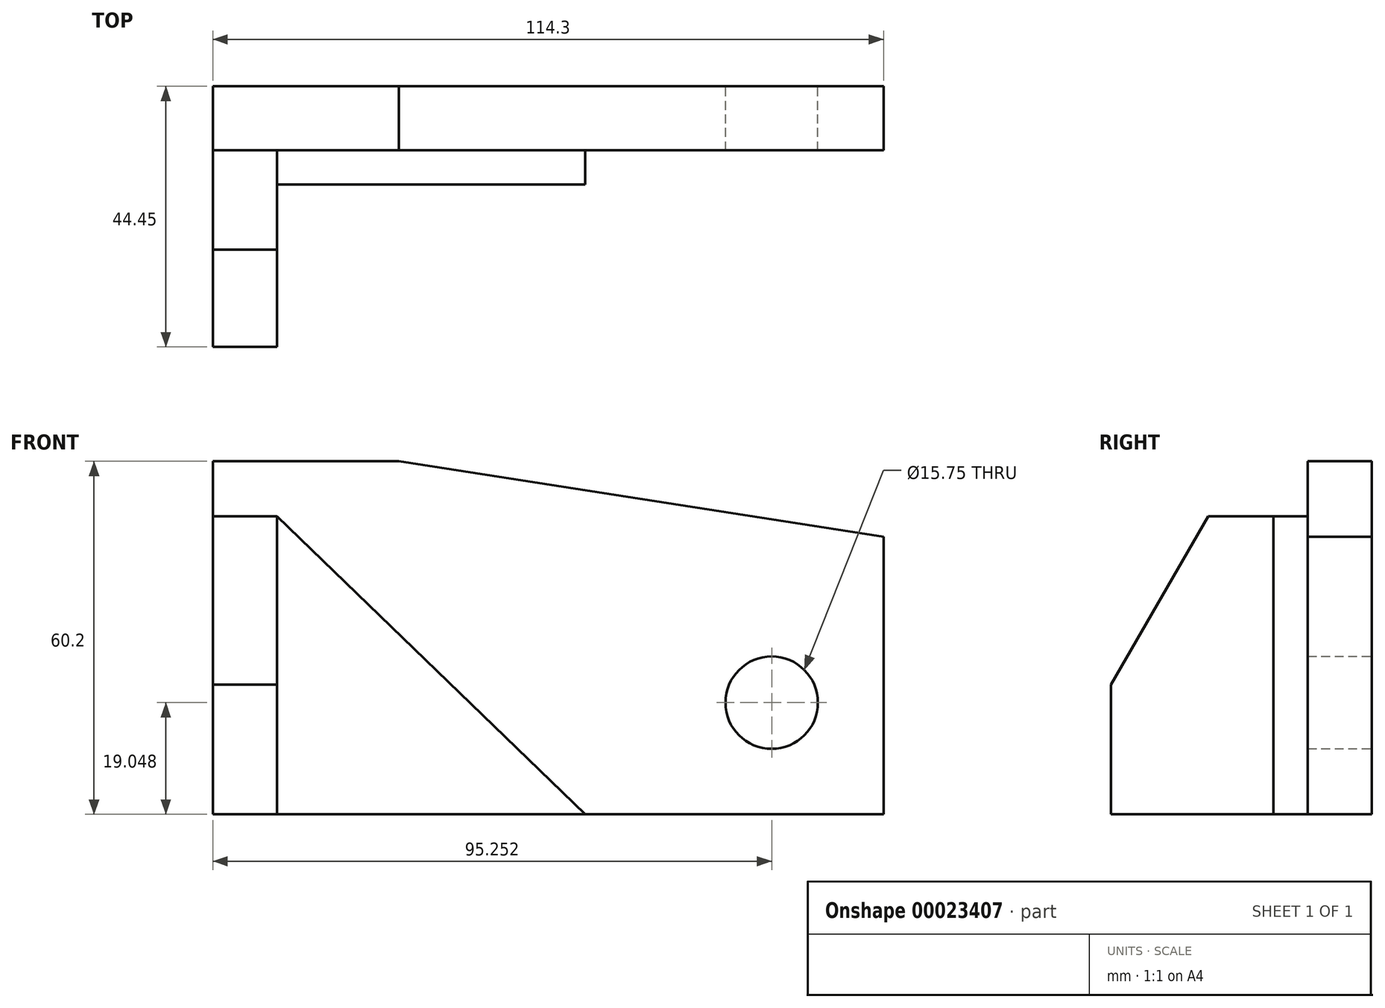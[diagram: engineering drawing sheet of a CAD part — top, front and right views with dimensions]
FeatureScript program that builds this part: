
annotation { "Feature Type Name" : "Feature", "Feature Type Description" : "" }
export const myFeature = defineFeature(function(context is Context, id is Id, definition is map)
    precondition{}
    {
        {
            var Q0;
            Q0=qCreatedBy(makeId("Front.planeOp"),FACE);
            var sketch = newSketch(context, id + "F0", { "sketchPlane" : qUnion([Q0])});
            skLineSegment(sketch, "E0.bottom", {"start": v(-74.75, 28.99) * mm, "end": v(-43, 28.99) * mm});
            skLineSegment(sketch, "E0.top", {"start": v(-74.75, -31.21) * mm, "end": v(39.55, -31.21) * mm});
            skLineSegment(sketch, "E0.left", {"start": v(-74.75, 28.99) * mm, "end": v(-74.75, -31.21) * mm});
            skLineSegment(sketch, "E0.right", {"start": v(39.55, 16.13) * mm, "end": v(39.55, -31.21) * mm});
            skLineSegment(sketch, "E1", {"start": v(-43, 28.99) * mm, "end": v(39.55, 16.13) * mm});
            skLineSegment(sketch, "E2", {"start": v(39.55, -12.16) * mm, "end": v(20.5, -12.16) * mm});
            skLineSegment(sketch, "E3", {"start": v(20.5, -12.16) * mm, "end": v(20.5, -31.21) * mm});
            skCircle(sketch, "E4", {"center": v(20.5, -12.16) * mm, "radius": 7.87 * mm});
            skSolve(sketch);
        }
        {
            var Q0;
            Q0 = qSketchRegion(id + "F0", true);
            extrude(context, id + "F1", {"entities" : qUnion([Q0]), "depth" : 10.92 * mm});
        }
        {
            var Q0;
            Q0=makeQuery(id+"F1.opExtrude","SWEPT_FACE",FACE,{"disambiguationData":[OSD([sQuery(id+"F0.wireOp",EDGE,"E0.left")])]});
            var sketch = newSketch(context, id + "F2", { "sketchPlane" : qUnion([Q0])});
            skLineSegment(sketch, "E5.bottom", {"start": v(10.92, 19.62) * mm, "end": v(27.88, 19.62) * mm});
            skLineSegment(sketch, "E5.top", {"start": v(10.92, -31.18) * mm, "end": v(44.45, -31.18) * mm});
            skLineSegment(sketch, "E5.left", {"start": v(10.92, 19.62) * mm, "end": v(10.92, -31.18) * mm});
            skLineSegment(sketch, "E5.right", {"start": v(44.45, -9.08) * mm, "end": v(44.45, -31.18) * mm});
            skLineSegment(sketch, "E6", {"start": v(27.88, 19.62) * mm, "end": v(44.45, -9.08) * mm});
            skLineSegment(sketch, "E7", {"start": v(44.45, -31.18) * mm, "end": v(44.45, -9.08) * mm});
            skSolve(sketch);
        }
        {
            var Q0;
            Q0=makeQuery(id+"F2.imprint","IMPRINT",FACE,{"disambiguationData":[TD([[makeQuery(id+"F2.imprint","IMPRINT",EDGE,{"derivedFrom":sQuery(id+"F2.wireOp",EDGE,"E5.bottom")}),-1.0]])]});
            extrude(context, id + "F3", {"entities" : qUnion([Q0]), "oppositeDirection" : true, "depth" : 10.92 * mm});
        }
        {
            var Q0;
            Q0=makeQuery(id+"F1.opExtrude","CAP_FACE",FACE,{"disambiguationData":[OSD([sQuery(id+"F0.wireOp",EDGE,"E0.bottom"),sQuery(id+"F0.wireOp",EDGE,"E0.top"),sQuery(id+"F0.wireOp",EDGE,"E0.left"),sQuery(id+"F0.wireOp",EDGE,"E0.right"),sQuery(id+"F0.wireOp",EDGE,"E1"),sQuery(id+"F0.wireOp",EDGE,"E4")])],"isStart":false});
            var sketch = newSketch(context, id + "F4", { "sketchPlane" : qUnion([Q0])});
            skLineSegment(sketch, "E8", {"start": v(-11.25, -31.21) * mm, "end": v(-63.83, 19.59) * mm});
            skLineSegment(sketch, "E9", {"start": v(-11.25, -31.21) * mm, "end": v(-74.75, -31.21) * mm});
            skLineSegment(sketch, "E10", {"start": v(-63.83, 19.59) * mm, "end": v(-63.83, -31.21) * mm});
            skLineSegment(sketch, "E11", {"start": v(-11.25, -31.21) * mm, "end": v(-63.83, -31.21) * mm});
            skSolve(sketch);
        }
        {
            var Q0;
            Q0 = qSketchRegion(id + "F4", true);
            extrude(context, id + "F5", {"entities" : qUnion([Q0]), "depth" : 5.84 * mm});
        }
    });
